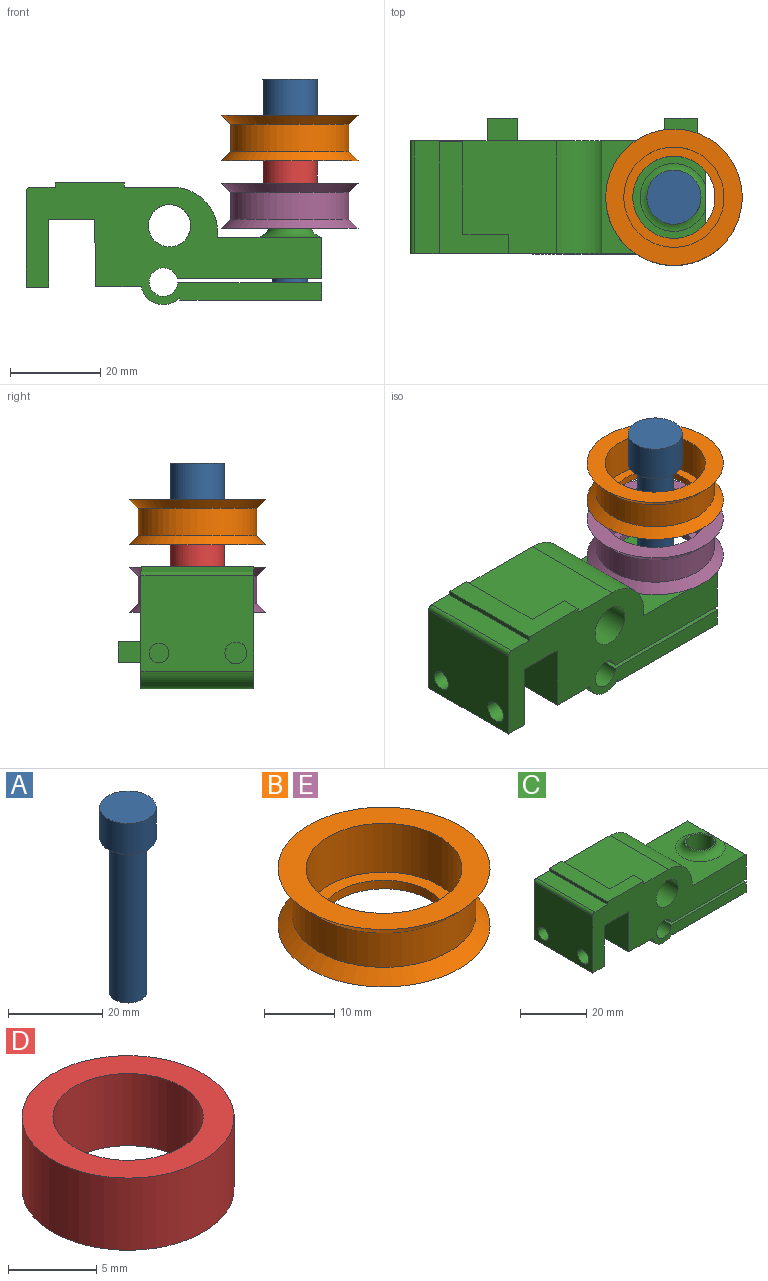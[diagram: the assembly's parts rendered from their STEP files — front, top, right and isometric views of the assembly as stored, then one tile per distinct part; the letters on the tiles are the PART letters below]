
ASSEMBLY  parts=5 mates=4
PART A: 5 faces, bbox 12x12x48 mm
  f0: cylinder r=4mm len=40mm, axis (0,0,-1), area 1005.3mm2, adj f1,f4
  f1: plane 8x8mm, normal (0,0,-1), area 50.3mm2, adj f0
  f2: cylinder r=6mm len=12mm, axis (0,0,-1), area 301.6mm2, adj f3,f4
  f3: plane 12x12mm, normal (0,0,1), area 113.1mm2, adj f2
  f4: plane 12x12mm, normal (0,0,-1), area 62.8mm2, adj f0,f2
PART B: 8 faces, bbox 30.2x30.2x10 mm
  f0: plane 30.2x30.2mm, normal (0,0,1), area 329.2mm2, adj f1,f7
  f1: cylinder r=11.1mm len=22.2mm, axis (0,0,-1), area 592.8mm2, adj f0,f2
  f2: plane 22.2x22.2mm, normal (0,0,1), area 126.9mm2, adj f1,f3
  f3: cylinder r=9.1mm len=18.2mm, axis (0,0,-1), area 85.8mm2, adj f2,f4
  f4: plane 30.2x30.2mm, normal (0,0,-1), area 456.2mm2, adj f3,f5
  f5: cone r=13.1mm half-angle=45deg, axis (0,0,-1), area 250.6mm2, adj f4,f6
  f6: cylinder r=13.1mm len=26.2mm, axis (0,0,-1), area 493.9mm2, adj f5,f7
  f7: cone r=15.1mm half-angle=45deg, axis (0,0,1), area 250.6mm2, adj f0,f6
PART C: 43 faces, bbox 68.9x30x27 mm
  f0: plane 25x3.86mm, normal (1,0,0), area 96.5mm2, adj f4,f14,f15,f19
  f1: cylinder r=4.17mm len=8.35mm, axis (0,0,1), area 101.3mm2, adj f4,f19
  f2: plane 25x10.1mm, normal (0,0,-1), area 252.6mm2, adj f13,f14,f15,f17
  f3: plane 25x0.6mm, normal (-1,0,0), area 14.9mm2, adj f4,f14,f15,f17
  f4: plane 31.35x25mm, normal (0,0,-1), area 729mm2, adj f0,f1,f3,f14,f15
  f5: plane 25x9.08mm, normal (1,0,0), area 226.1mm2, adj f6,f14,f15,f20,f24
  f6: plane 25x23mm, normal (0,0,1), area 400mm2, adj f5,f7,f14,f15,f24
  f7: plane 25x1.1mm, normal (1,0,0), area 27.5mm2, adj f6,f14,f15,f25
  f8: plane 31.42x25mm, normal (0,0,1), area 611.6mm2, adj f14,f15,f25,f27,f37,f38,f39,f40
  f9: plane 25x21.09mm, normal (-1,0,0), area 493.5mm2, adj f10,f14,f15,f22,f23,f27
  f10: plane 25x5mm, normal (0,0,-1), area 125mm2, adj f9,f11,f14,f15
  f11: plane 25x15mm, normal (1,0,0), area 341.3mm2, adj f10,f12,f14,f15,f22,f23
  f12: plane 25x10.2mm, normal (0,0,-1), area 255mm2, adj f11,f13,f14,f15
  f13: plane 25x14.91mm, normal (-1,0,-0.01), area 372.8mm2, adj f2,f12,f14,f15
  f14: plane 65.42x27mm, normal (0,-1,0), area 1014.1mm2, adj f0,f2,f3,f4,f5,f6,f7,f8
  f15: plane 65.42x26mm, normal (0,1,0), area 938.8mm2, adj f0,f2,f3,f4,f5,f6,f7,f8
  f16: cylinder r=4.17mm len=11.04mm, axis (0,0,1), area 289.6mm2, adj f20,f21
  f17: cylinder r=5mm len=25mm, axis (0,-1,0), area 273.8mm2, adj f2,f3,f14,f15
  f18: cylinder r=3.15mm len=25mm, axis (0,-1,0), area 469.5mm2, adj f14,f15,f19,f20
  f19: plane 31.86x25mm, normal (0,0,1), area 741.8mm2, adj f0,f1,f14,f15,f18
  f20: plane 31.98x30mm, normal (0,0,-1), area 781.2mm2, adj f5,f14,f15,f16,f18,f29,f30,f31
  f21: plane 9.35x9.35mm, normal (0,0,1), area 13.9mm2, adj f16,f24
  f22: cylinder r=2.43mm len=5mm, axis (-1,0,0), area 76.2mm2, adj f9,f11
  f23: cylinder r=2.2mm len=5mm, axis (-1,0,0), area 69.1mm2, adj f9,f11
  f24: torus R=7.5mm, axis (0,0,-1), area 134.6mm2, adj f5,f6,f21
  f25: cylinder r=10mm len=25mm, axis (0,-1,0), area 392.7mm2, adj f7,f8,f14,f15
  f26: cylinder r=4.68mm len=25mm, axis (0,-1,0), area 735.2mm2, adj f14,f15
  f27: cylinder r=1mm len=25mm, axis (0,-1,0), area 39.3mm2, adj f8,f9,f14,f15
  f28: plane 7.3x5mm, normal (0,0,1), area 36.5mm2, adj f15,f29,f30,f31
  f29: plane 5x4.12mm, normal (1,0,0), area 20.6mm2, adj f15,f20,f28,f31
  f30: plane 5x4.12mm, normal (-1,0,0), area 20.6mm2, adj f15,f20,f28,f31
  f31: plane 7.3x4.12mm, normal (0,1,0), area 30.1mm2, adj f20,f28,f29,f30
  f32: plane 6.63x5mm, normal (0,0,1), area 33.2mm2, adj f15,f33,f35,f36
  f33: plane 5x4.5mm, normal (1,0,0), area 22.5mm2, adj f15,f32,f34,f36
  f34: plane 6.63x5mm, normal (0,0,-1), area 33.2mm2, adj f15,f33,f35,f36
  f35: plane 5x4.5mm, normal (-1,0,0), area 22.5mm2, adj f15,f32,f34,f36
  f36: plane 6.63x4.5mm, normal (0,1,0), area 29.9mm2, adj f32,f33,f34,f35
  f37: plane 24.79x1mm, normal (-1,0,0), area 24.8mm2, adj f8,f14,f41,f42
  f38: plane 4.34x1mm, normal (1,0,0), area 4.3mm2, adj f8,f14,f39,f42
  f39: plane 10.05x1mm, normal (0,1,0), area 10.1mm2, adj f8,f38,f40,f42
  f40: plane 20.45x1mm, normal (1,0,0), area 20.4mm2, adj f8,f39,f41,f42
  f41: plane 5.26x1mm, normal (0,1,0), area 5.3mm2, adj f8,f37,f40,f42
  f42: plane 24.79x15.31mm, normal (0,0,1), area 174mm2, adj f14,f37,f38,f39,f40,f41
PART D: 4 faces, bbox 12x12x5 mm
  f0: cylinder r=4.25mm len=8.5mm, axis (0,0,-1), area 133.5mm2, adj f2,f3
  f1: cylinder r=6mm len=12mm, axis (0,0,-1), area 188.5mm2, adj f2,f3
  f2: plane 12x12mm, normal (0,0,1), area 56.4mm2, adj f0,f1
  f3: plane 12x12mm, normal (0,0,-1), area 56.4mm2, adj f0,f1
PART E: same geometry as B
PLACE A t=(23.78,-12.5,-2.1)mm
PLACE B t=(23.78,-12.5,33.1)mm
PLACE C at identity
PLACE D rot(axis=(1,0,0),180deg) t=(23.78,-12.5,27.9)mm
PLACE E t=(23.78,-12.5,18.1)mm
MATE fastened D.f0 <-> E.f1  axis (0,0,1) through (23.78,-12.5,22.9)mm
MATE fastened A.f0 <-> B.f1  axis (0,0,-1) through (23.78,-12.5,37.9)mm
MATE fastened B.f1 <-> E.f1  axis (0,0,-1) through (23.78,-12.5,27.9)mm
MATE fastened E.f1 <-> C.f1  axis (0,0,-1) through (23.78,-12.5,12.9)mm
